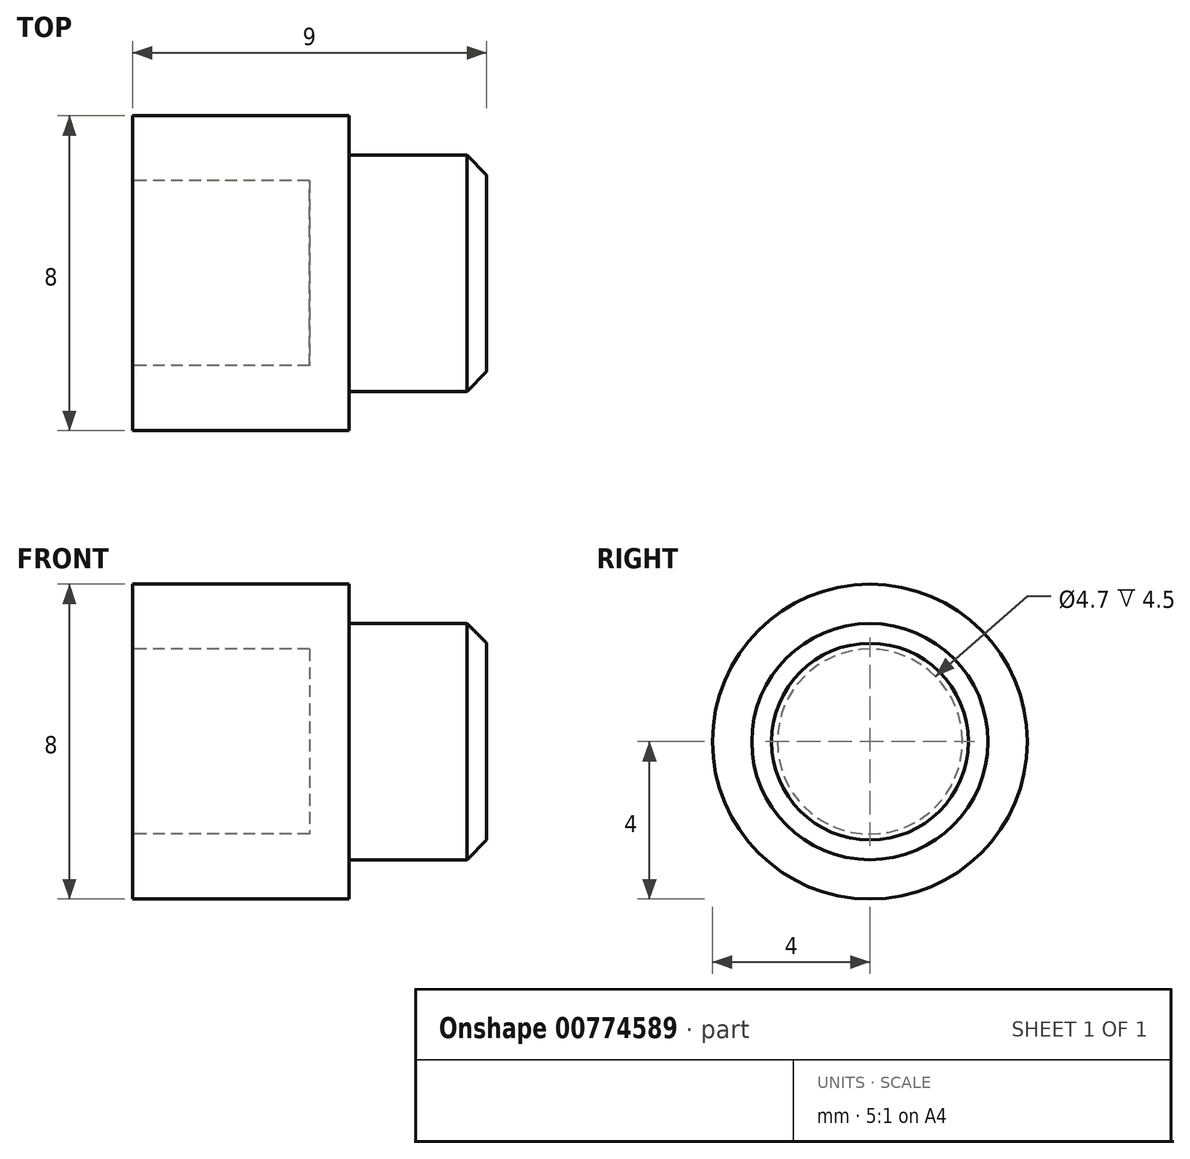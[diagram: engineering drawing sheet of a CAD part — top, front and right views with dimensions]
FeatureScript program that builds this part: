
annotation { "Feature Type Name" : "Feature", "Feature Type Description" : "" }
export const myFeature = defineFeature(function(context is Context, id is Id, definition is map)
    precondition{}
    {
        {
            var Q0;
            Q0=qCreatedBy(makeId("Front.planeOp"),FACE);
            var sketch = newSketch(context, id + "F0", { "sketchPlane" : qUnion([Q0])});
            skLineSegment(sketch, "E0", {"start": v(-16.33, 0) * mm, "end": v(17.52, 0) * mm, "construction": true});
            skLineSegment(sketch, "E1", {"start": v(0, 0) * mm, "end": v(0, 3) * mm});
            skLineSegment(sketch, "E2", {"start": v(0, 3) * mm, "end": v(-3.5, 3) * mm});
            skLineSegment(sketch, "E3", {"start": v(-3.5, 3) * mm, "end": v(-3.5, 4) * mm});
            skLineSegment(sketch, "E4", {"start": v(-3.5, 4) * mm, "end": v(-9, 4) * mm});
            skLineSegment(sketch, "E5", {"start": v(-9, 4) * mm, "end": v(-9, 2.35) * mm});
            skLineSegment(sketch, "E6", {"start": v(-9, 2.35) * mm, "end": v(-4.5, 2.35) * mm});
            skLineSegment(sketch, "E7", {"start": v(-4.5, 2.35) * mm, "end": v(-4.5, 0) * mm});
            skLineSegment(sketch, "E8", {"start": v(-4.5, 0) * mm, "end": v(0, 0) * mm});
            skSolve(sketch);
        }
        {
            var Q0;
            Q0=makeQuery(id+"F0.imprint","IMPRINT",FACE,{"disambiguationData":[TD([[makeQuery(id+"F0.imprint","IMPRINT",EDGE,{"derivedFrom":sQuery(id+"F0.wireOp",EDGE,"E1")}),1.0]])]});
            var Q1;
            Q1=sQuery(id+"F0.wireOp",EDGE,"E0");
            revolve(context, id + "F1", {"surfaceOperationType" : NewSurfaceOperationType.NEW, "entities" : qUnion([Q0]), "axis" : qUnion([Q1]), "revolveType" : RevolveType.FULL});
        }
        {
            var Q0;
            Q0=makeQuery(id+"F1.opRevolve","SWEPT_EDGE",EDGE,{"disambiguationData":[OSD([sQuery(id+"F0.wireOp",EDGE,"E1"),sQuery(id+"F0.wireOp",EDGE,"E2")])]});
            chamfer(context, id + "F2", {"entities" : qUnion([Q0]), "width" : .5 * mm, "tangentPropagation" : true});
        }
    });
